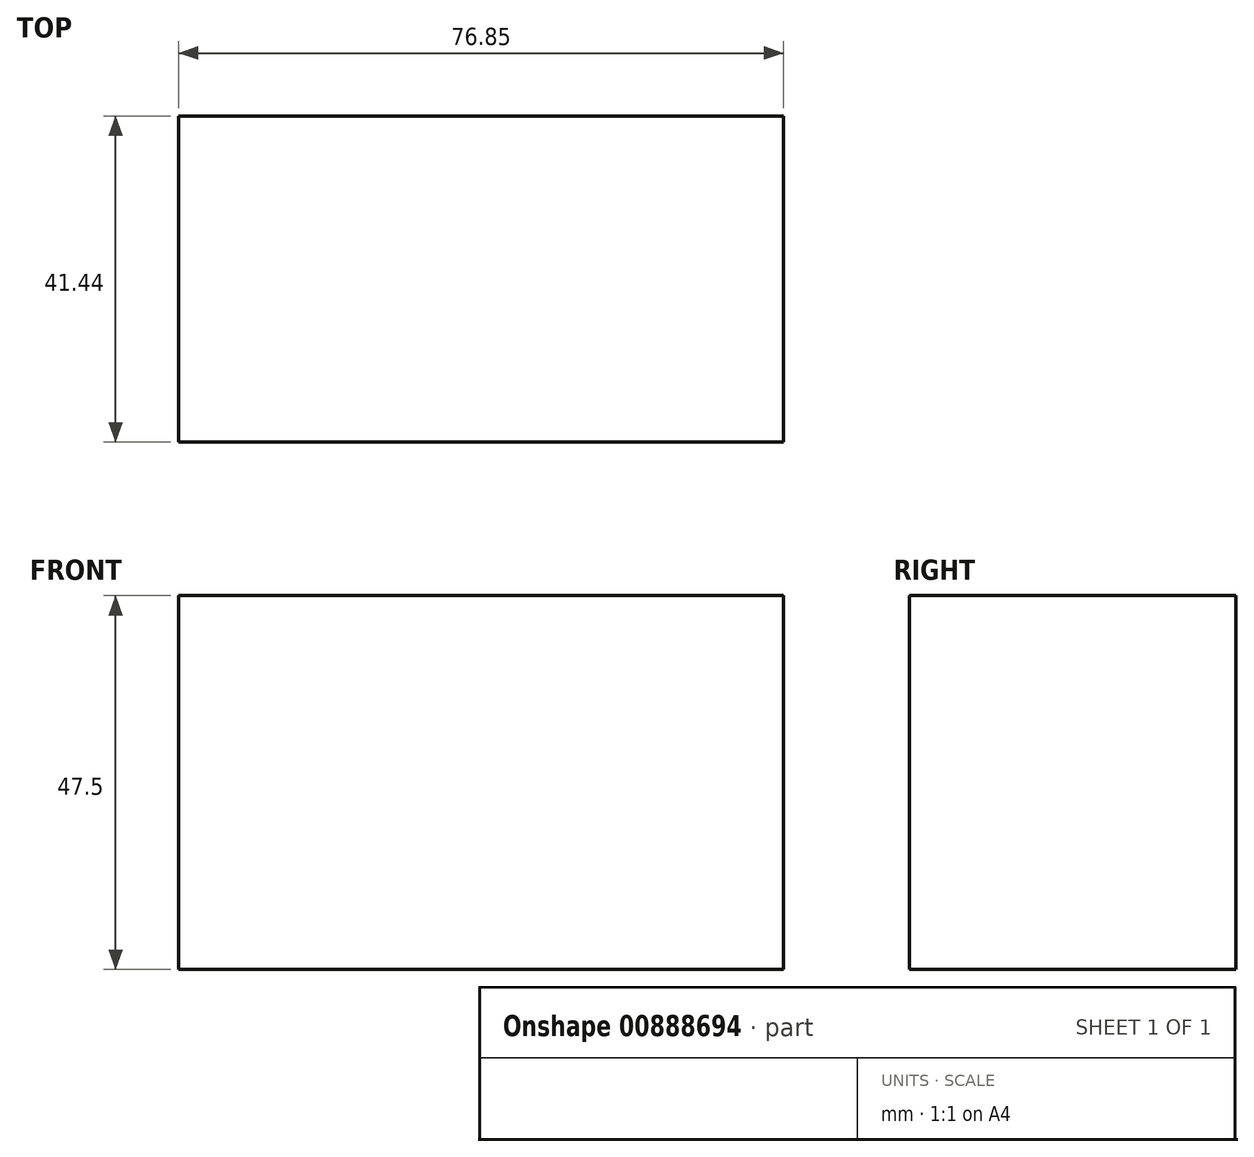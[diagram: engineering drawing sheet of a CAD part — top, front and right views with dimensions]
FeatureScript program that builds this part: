
annotation { "Feature Type Name" : "Feature", "Feature Type Description" : "" }
export const myFeature = defineFeature(function(context is Context, id is Id, definition is map)
    precondition{}
    {
        {
            var Q0;
            Q0=qCreatedBy(makeId("Top.planeOp"),FACE);
            var sketch = newSketch(context, id + "F0", { "sketchPlane" : qUnion([Q0])});
            skLineSegment(sketch, "E0.bottom", {"start": v(-28.35, 15.97) * mm, "end": v(48.5, 15.97) * mm});
            skLineSegment(sketch, "E0.top", {"start": v(-28.35, -25.47) * mm, "end": v(48.5, -25.47) * mm});
            skLineSegment(sketch, "E0.left", {"start": v(-28.35, 15.97) * mm, "end": v(-28.35, -25.47) * mm});
            skLineSegment(sketch, "E0.right", {"start": v(48.5, 15.97) * mm, "end": v(48.5, -25.47) * mm});
            skSolve(sketch);
        }
        {
            var Q0;
            Q0 = qSketchRegion(id + "F0", true);
            extrude(context, id + "F1", {"entities" : qUnion([Q0]), "depth" : 47.5 * mm, "offsetDistance" : 25.4 * mm});
        }
    });
